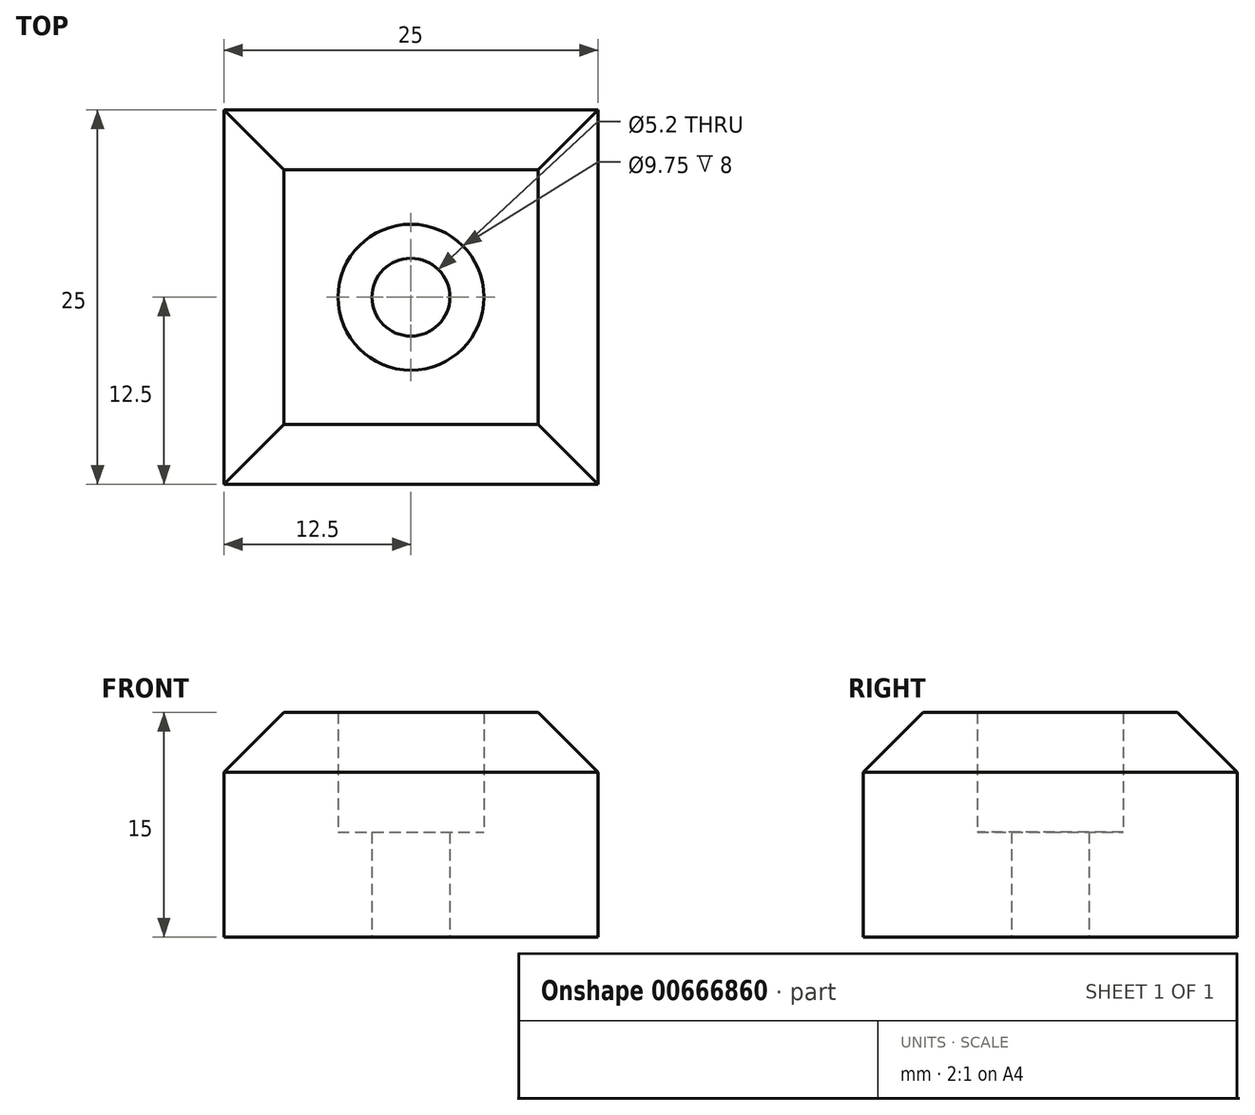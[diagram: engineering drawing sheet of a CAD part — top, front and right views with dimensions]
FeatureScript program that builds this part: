
annotation { "Feature Type Name" : "Feature", "Feature Type Description" : "" }
export const myFeature = defineFeature(function(context is Context, id is Id, definition is map)
    precondition{}
    {
        {
            var Q0;
            Q0=qCreatedBy(makeId("Top.planeOp"),FACE);
            var sketch = newSketch(context, id + "F0", { "sketchPlane" : qUnion([Q0])});
            skLineSegment(sketch, "E0.bottom", {"start": v(12.5, 12.5) * mm, "end": v(-12.5, 12.5) * mm});
            skLineSegment(sketch, "E0.top", {"start": v(12.5, -12.5) * mm, "end": v(-12.5, -12.5) * mm});
            skLineSegment(sketch, "E0.left", {"start": v(12.5, 12.5) * mm, "end": v(12.5, -12.5) * mm});
            skLineSegment(sketch, "E0.right", {"start": v(-12.5, 12.5) * mm, "end": v(-12.5, -12.5) * mm});
            skPoint(sketch, "E0.middle", {"position": v(0, 0) * mm});
            skSolve(sketch);
        }
        {
            var Q0;
            Q0=makeQuery(id+"F0.imprint","IMPRINT",FACE,{"disambiguationData":[TD([[makeQuery(id+"F0.imprint","IMPRINT",EDGE,{"derivedFrom":sQuery(id+"F0.wireOp",EDGE,"E0.bottom")}),1.0]])]});
            extrude(context, id + "F1", {"entities" : qUnion([Q0]), "depth" : 15 * mm, "offsetDistance" : 25 * mm});
        }
        {
            var Q0;
            Q0=makeQuery(id+"F1.opExtrude","CAP_EDGE",EDGE,{"disambiguationData":[OSD([sQuery(id+"F0.wireOp",EDGE,"E0.right")])],"isStart":false});
            var Q1;
            Q1=makeQuery(id+"F1.opExtrude","CAP_EDGE",EDGE,{"disambiguationData":[OSD([sQuery(id+"F0.wireOp",EDGE,"E0.bottom")])],"isStart":false});
            var Q2;
            Q2=makeQuery(id+"F1.opExtrude","CAP_EDGE",EDGE,{"disambiguationData":[OSD([sQuery(id+"F0.wireOp",EDGE,"E0.left")])],"isStart":false});
            var Q3;
            Q3=makeQuery(id+"F1.opExtrude","CAP_EDGE",EDGE,{"disambiguationData":[OSD([sQuery(id+"F0.wireOp",EDGE,"E0.top")])],"isStart":false});
            chamfer(context, id + "F2", {"entities" : qUnion([Q0, Q1, Q2, Q3]), "width" : 4 * mm, "tangentPropagation" : true});
        }
        {
            var Q0;
            Q0=makeQuery(id+"F1.opExtrude","CAP_FACE",FACE,{"disambiguationData":[OSD([sQuery(id+"F0.wireOp",EDGE,"E0.bottom"),sQuery(id+"F0.wireOp",EDGE,"E0.top"),sQuery(id+"F0.wireOp",EDGE,"E0.left"),sQuery(id+"F0.wireOp",EDGE,"E0.right")])],"isStart":false});
            var sketch = newSketch(context, id + "F3", { "sketchPlane" : qUnion([Q0])});
            skLineSegment(sketch, "E1", {"start": v(-8.5, 0) * mm, "end": v(8.5, 0) * mm, "construction": true});
            skPoint(sketch, "E2", {"position": v(0, 0) * mm});
            skSolve(sketch);
        }
        {
            var Q0;
            Q0=sQuery(id+"F3.wireOp",VERTEX,"E2");
            var Q1;
            Q1=makeQuery(id+"F1.opExtrude","SWEPT_BODY",BODY,{"disambiguationData":[OSD([sQuery(id+"F0.wireOp",EDGE,"E0.bottom"),sQuery(id+"F0.wireOp",EDGE,"E0.top"),sQuery(id+"F0.wireOp",EDGE,"E0.left"),sQuery(id+"F0.wireOp",EDGE,"E0.right")])]});
            hole(context, id + "F4", {"style" : HoleStyle.C_BORE, "endStyle" : HoleEndStyle.THROUGH, "holeDiameter" : 5.2 * mm, "cBoreDiameter" : 9.75 * mm, "cBoreDepth" : 8 * mm, "majorDiameter" : 5 * mm, "isTappedThrough" : true, "tappedDepth" : 12 * mm, "tapClearance" : 3, "locations" : qUnion([Q0]), "scope" : qUnion([Q1])});
        }
    });
